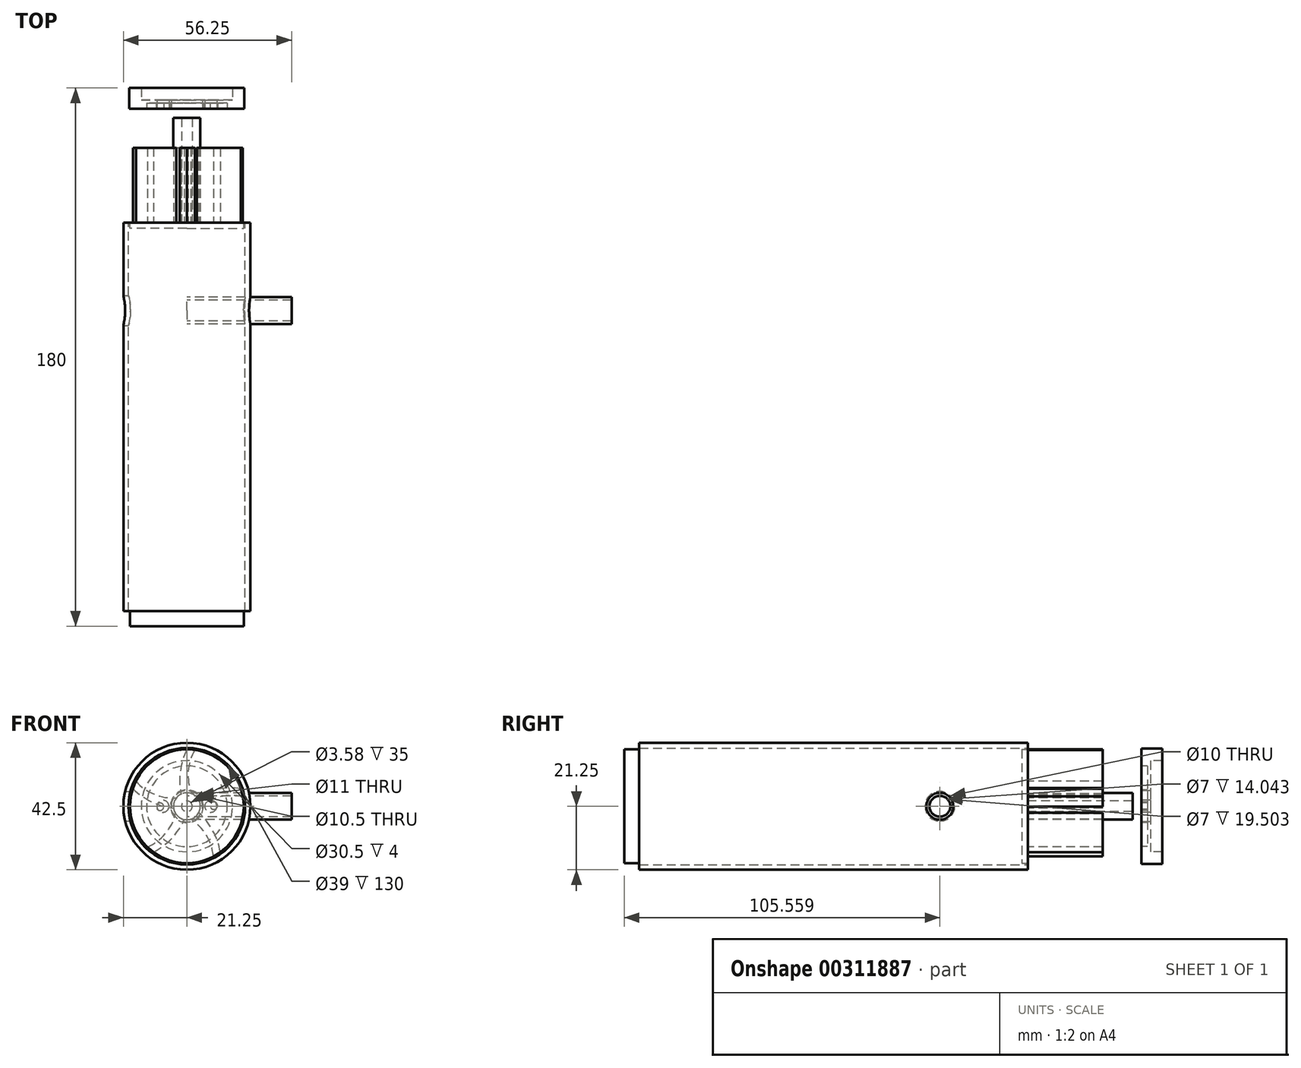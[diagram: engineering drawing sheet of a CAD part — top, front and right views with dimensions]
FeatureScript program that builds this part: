
annotation { "Feature Type Name" : "Feature", "Feature Type Description" : "" }
export const myFeature = defineFeature(function(context is Context, id is Id, definition is map)
    precondition{}
    {
        {
            var Q0;
            Q0=qCreatedBy(makeId("Front.planeOp"),FACE);
            var sketch = newSketch(context, id + "F0", { "sketchPlane" : qUnion([Q0])});
            skCircle(sketch, "E0", {"center": v(0, 0) * mm, "radius": 19.5 * mm});
            skCircle(sketch, "E1", {"center": v(0, 0) * mm, "radius": 21.25 * mm});
            skSolve(sketch);
        }
        {
            var Q0;
            Q0 = qSketchRegion(id + "F0", true);
            extrude(context, id + "F1", {"entities" : qUnion([Q0]), "depth" : 130 * mm});
        }
        {
            var Q0;
            Q0=qCreatedBy(makeId("Front.planeOp"),FACE);
            var sketch = newSketch(context, id + "F2", { "sketchPlane" : qUnion([Q0])});
            skCircle(sketch, "E2", {"center": v(0, 0) * mm, "radius": 19 * mm});
            skSolve(sketch);
        }
        {
            var Q0;
            Q0 = qSketchRegion(id + "F2", true);
            extrude(context, id + "F3", {"entities" : qUnion([Q0]), "depth" : 2 * mm});
        }
        {
            var Q0;
            Q0=qCreatedBy(makeId("Right.planeOp"),FACE);
            var sketch = newSketch(context, id + "F4", { "sketchPlane" : qUnion([Q0])});
            skLineSegment(sketch, "E3", {"start": v(0, 0) * mm, "end": v(26.05, 0) * mm, "construction": true});
            skSolve(sketch);
        }
        {
            var Q0;
            Q0=makeQuery(id+"F3.opExtrude","CAP_FACE",FACE,{"disambiguationData":[OSD([sQuery(id+"F2.wireOp",EDGE,"E2")])],"isStart":true});
            var sketch = newSketch(context, id + "F5", { "sketchPlane" : qUnion([Q0])});
            skCircle(sketch, "E4", {"center": v(0, 0) * mm, "radius": 4 * mm});
            skArc(sketch, "E5", {"start": v(-1.82, 3.56) * mm, "mid": v(-0.43, 11.29) * mm, "end": v(-2.7, 18.8) * mm});
            skArc(sketch, "E6", {"start": v(1.82, 3.56) * mm, "mid": v(2.25, 11.44) * mm, "end": v(0, 19) * mm});
            skSolve(sketch);
        }
        {
            var Q0;
            {var subQ0=sQuery(id+"F5.wireOp",EDGE,"E5");Q0=makeQuery(id+"F5.imprint","IMPRINT",FACE,{"disambiguationData":[TD([[makeQuery(id+"F5.imprint","IMPRINT",EDGE,{"derivedFrom":subQ0}),-1.0]])]});}
            extrude(context, id + "F6", {"entities" : qUnion([Q0]), "operationType" : NewBodyOperationType.ADD, "depth" : 25 * mm});
        }
        {
            var Q0;
            Q0=makeQuery(id+"F3.opExtrude","SWEPT_BODY",BODY,{"disambiguationData":[OSD([sQuery(id+"F2.wireOp",EDGE,"E2")])]});
            var Q1;
            Q1=sQuery(id+"F4.wireOp",EDGE,"E3");
            circularPattern(context, id + "F7", {"entities" : qUnion([Q0]), "axis" : qUnion([Q1]), "angle" : 360 * degree, "instanceCount" : 5, "equalSpace" : true});
        }
        {
            var Q0;
            Q0=qCreatedBy(makeId("Front.planeOp"),FACE);
            var sketch = newSketch(context, id + "F8", { "sketchPlane" : qUnion([Q0])});
            skCircle(sketch, "E7", {"center": v(0, 0) * mm, "radius": 1.8 * mm});
            skCircle(sketch, "E8", {"center": v(0, 0) * mm, "radius": 4.5 * mm});
            skSolve(sketch);
        }
        {
            var Q0;
            Q0 = qSketchRegion(id + "F8", true);
            extrude(context, id + "F9", {"entities" : qUnion([Q0]), "operationType" : NewBodyOperationType.ADD, "oppositeDirection" : true, "depth" : 35 * mm});
        }
        {
            var Q0;
            {var subQ0=sQuery(id+"F5.wireOp",EDGE,"E5");Q0=makeQuery(id+"F5.imprint","IMPRINT",FACE,{"disambiguationData":[TD([[makeQuery(id+"F5.imprint","IMPRINT",EDGE,{"derivedFrom":subQ0}),1.0]])]});}
            cPlane(context, id + "F10", {"entities" : qUnion([Q0]), "cplaneType" : CPlaneType.OFFSET, "offset" : 38 * mm, "width" : 150 * mm, "height" : 150 * mm});
        }
        {
            var Q0;
            Q0=qCreatedBy(id+"F10.planeOp",FACE);
            var sketch = newSketch(context, id + "F11", { "sketchPlane" : qUnion([Q0])});
            skCircle(sketch, "E9", {"center": v(0, 0) * mm, "radius": 13.5 * mm});
            skCircle(sketch, "E10", {"center": v(0, 0) * mm, "radius": 5.5 * mm});
            skCircle(sketch, "E11", {"center": v(0, 0) * mm, "radius": 9 * mm, "construction": true});
            skCircle(sketch, "E12", {"center": v(9, -0.15) * mm, "radius": 1.25 * mm});
            skCircle(sketch, "E13", {"center": v(-9, 0.2) * mm, "radius": 1.25 * mm});
            skSolve(sketch);
        }
        {
            var Q0;
            Q0 = qSketchRegion(id + "F11", true);
            extrude(context, id + "F12", {"entities" : qUnion([Q0]), "depth" : 2 * mm});
        }
        {
            var Q0;
            Q0=makeQuery(id+"F1.opExtrude","CAP_FACE",FACE,{"disambiguationData":[OSD([sQuery(id+"F0.wireOp",EDGE,"E0"),sQuery(id+"F0.wireOp",EDGE,"E1")])],"isStart":false});
            var sketch = newSketch(context, id + "F13", { "sketchPlane" : qUnion([Q0])});
            skCircle(sketch, "E14", {"center": v(0, 0) * mm, "radius": 19 * mm});
            skSolve(sketch);
        }
        {
            var Q0;
            Q0=makeQuery(id+"F13.imprint","IMPRINT",FACE,{"disambiguationData":[TD([[makeQuery(id+"F13.imprint","IMPRINT",EDGE,{"derivedFrom":sQuery(id+"F13.wireOp",EDGE,"E14")}),1.0]])]});
            extrude(context, id + "F14", {"entities" : qUnion([Q0]), "depth" : 5 * mm});
        }
        {
            var Q0;
            Q0=qCreatedBy(id+"F10.planeOp",FACE);
            var sketch = newSketch(context, id + "F15", { "sketchPlane" : qUnion([Q0])});
            skCircle(sketch, "E15", {"center": v(0, 0) * mm, "radius": 5.25 * mm});
            skCircle(sketch, "E16", {"center": v(-8, 0) * mm, "radius": 2 * mm});
            skCircle(sketch, "E17", {"center": v(8, 0) * mm, "radius": 2 * mm});
            skCircle(sketch, "E18", {"center": v(0, 0) * mm, "radius": 19.25 * mm});
            skSolve(sketch);
        }
        {
            var Q0;
            Q0=makeQuery(id+"F15.imprint","IMPRINT",FACE,{"disambiguationData":[TD([[makeQuery(id+"F15.imprint","IMPRINT",EDGE,{"derivedFrom":sQuery(id+"F15.wireOp",EDGE,"E15")}),-1.0]])]});
            var sketch = newSketch(context, id + "F16", { "sketchPlane" : qUnion([Q0])});
            skCircle(sketch, "E19", {"center": v(0, 0) * mm, "radius": 15.25 * mm});
            skCircle(sketch, "E20", {"center": v(0, 0) * mm, "radius": 19.25 * mm});
            skSolve(sketch);
        }
        {
            var Q0;
            Q0 = qSketchRegion(id + "F15", true);
            extrude(context, id + "F17", {"entities" : qUnion([Q0]), "depth" : 3 * mm});
        }
        {
            var Q0;
            Q0 = qSketchRegion(id + "F16", true);
            extrude(context, id + "F18", {"entities" : qUnion([Q0]), "operationType" : NewBodyOperationType.ADD, "depth" : 7 * mm});
        }
        {
            var Q0;
            Q0=qCreatedBy(makeId("Right.planeOp"),FACE);
            var sketch = newSketch(context, id + "F19", { "sketchPlane" : qUnion([Q0])});
            skLineSegment(sketch, "E21", {"start": v(-50.18, 0) * mm, "end": v(-16.53, 0) * mm, "construction": true});
            skCircle(sketch, "E22", {"center": v(-29.44, 0) * mm, "radius": 5 * mm});
            skSolve(sketch);
        }
        {
            var Q0;
            Q0 = qSketchRegion(id + "F19", true);
            extrude(context, id + "F20", {"entities" : qUnion([Q0]), "operationType" : NewBodyOperationType.REMOVE, "oppositeDirection" : true, "depth" : 25 * mm});
        }
        {
            var Q0;
            Q0=qCreatedBy(makeId("Right.planeOp"),FACE);
            var sketch = newSketch(context, id + "F21", { "sketchPlane" : qUnion([Q0])});
            skCircle(sketch, "E23", {"center": v(-29.44, 0) * mm, "radius": 4.5 * mm});
            skCircle(sketch, "E24", {"center": v(-29.44, 0) * mm, "radius": 3.5 * mm});
            skSolve(sketch);
        }
        {
            var Q0;
            Q0 = qSketchRegion(id + "F21", true);
            extrude(context, id + "F22", {"entities" : qUnion([Q0]), "operationType" : NewBodyOperationType.ADD, "depth" : 35 * mm});
        }
    });
